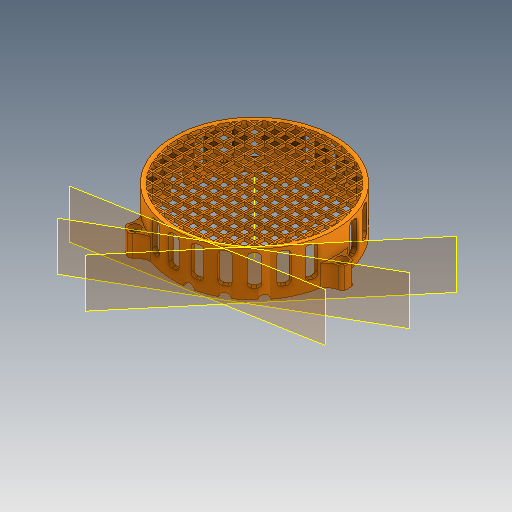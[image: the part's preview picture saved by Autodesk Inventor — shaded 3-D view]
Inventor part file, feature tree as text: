
AUTODESK INVENTOR PART (.ipt)
format: ipt  version: 2020.3 (Build 243373000, 373)  size: 1,752,064 bytes
history: native  units: mm
features: other x26, sketch x7
ambient origin geometry x8: Origin, YZ Plane, XZ Plane, XY Plane, X Axis, Y Axis, Z Axis, Center Point
bodies: Solid1 (feature_tree)
feature tree (33):
  other  "Scanner-TopPartV2.ipt"
  other  "Solid2::Scanner-TopPartV2.ipt"
  other  "TaggingFeature1"
  sketch  "Sketch1"  dims[d0=10.0mm]
  sketch  "Sketch8"
  sketch  "Sketch12"
  sketch  "Sketch13"
  sketch  "Sketch14"
  sketch  "Sketch15"
  sketch  "Sketch16"
  other  "Work Axis1"
  other  "Work Axis2"
  other  "Work Axis3"
  other  "Work Axis4"
  other  "Work Axis5"
  other  "Work Axis6"
  other  "Work Axis7"
  other  "Work Axis8"
  other  "Work Axis9"
  other  "Work Axis10"
  other  "Work Axis11"
  other  "Work Axis12"
  other  "Work Axis13"
  other  "Work Axis14"
  other  "Work Axis15"
  other  "Work Axis16"
  other  "Work Axis17"
  other  "Work Axis18"
  other  "Work Axis19"
  other  "Work Axis20"
  other  "Work Axis21"
  other  "Work Axis22"
  other  "Work Axis23"
